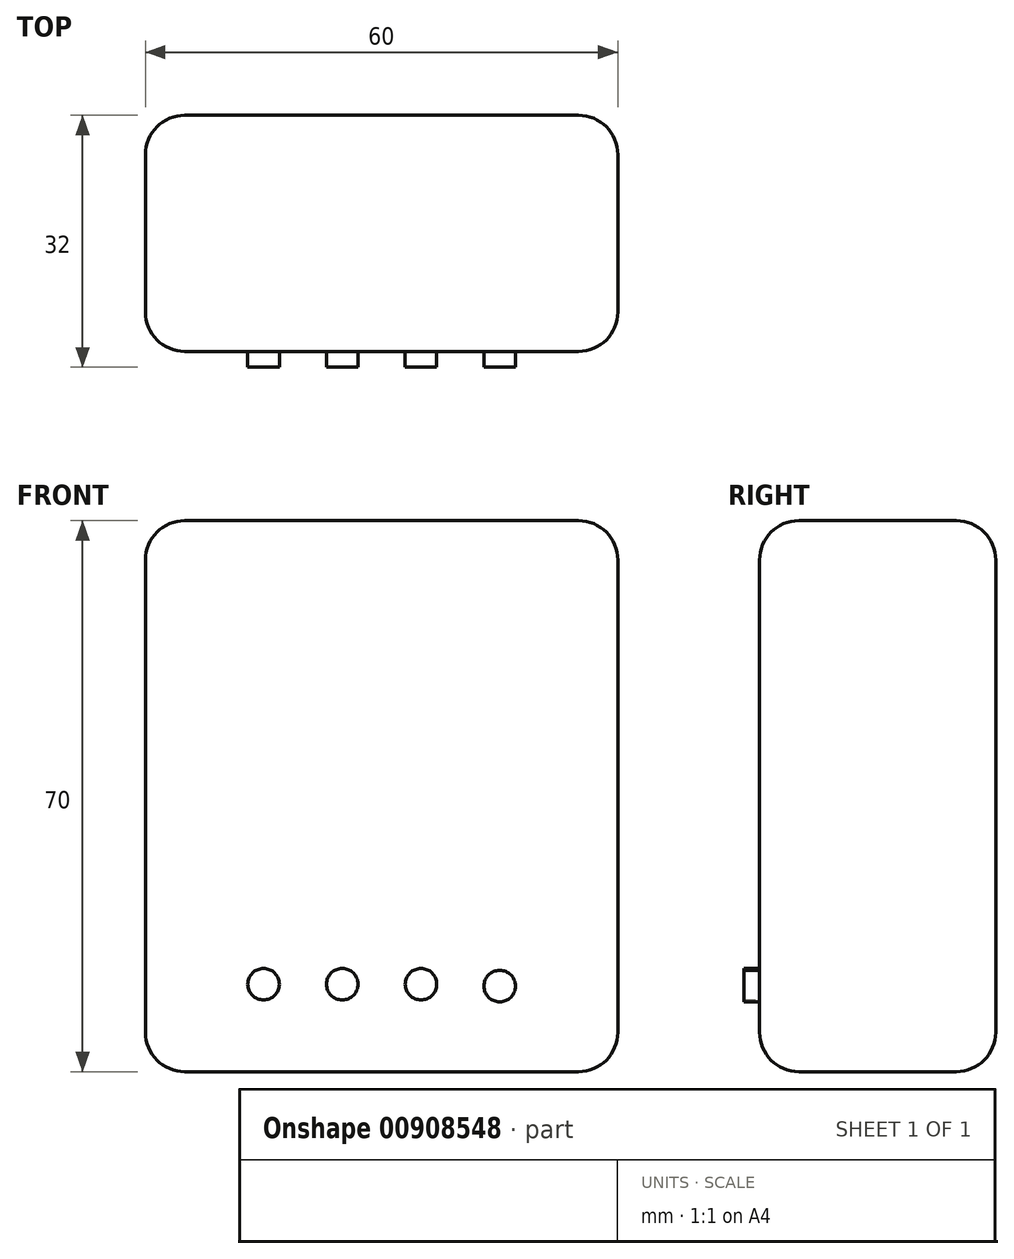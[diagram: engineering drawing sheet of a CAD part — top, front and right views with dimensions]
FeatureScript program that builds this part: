
annotation { "Feature Type Name" : "Feature", "Feature Type Description" : "" }
export const myFeature = defineFeature(function(context is Context, id is Id, definition is map)
    precondition{}
    {
        {
            var Q0;
            Q0=qCreatedBy(makeId("Front.planeOp"),FACE);
            var sketch = newSketch(context, id + "F0", { "sketchPlane" : qUnion([Q0])});
            skLineSegment(sketch, "E0.bottom", {"start": v(-30, 35) * mm, "end": v(30, 35) * mm});
            skLineSegment(sketch, "E0.top", {"start": v(-30, -35) * mm, "end": v(30, -35) * mm});
            skLineSegment(sketch, "E0.left", {"start": v(-30, 35) * mm, "end": v(-30, -35) * mm});
            skLineSegment(sketch, "E0.right", {"start": v(30, 35) * mm, "end": v(30, -35) * mm});
            skPoint(sketch, "E0.middle", {"position": v(0, 0) * mm});
            skPoint(sketch, "E1", {"position": v(-15, -23.89) * mm});
            skPoint(sketch, "E2", {"position": v(15, -24.13) * mm});
            skCircle(sketch, "E3", {"center": v(-15, -23.89) * mm, "radius": 2 * mm});
            skCircle(sketch, "E4", {"center": v(15, -24.13) * mm, "radius": 2 * mm});
            skCircle(sketch, "E5", {"center": v(-5, -23.89) * mm, "radius": 2 * mm});
            skCircle(sketch, "E6", {"center": v(5, -23.89) * mm, "radius": 2 * mm});
            skSolve(sketch);
        }
        {
            var Q0;
            Q0=makeQuery(id+"F0.imprint","IMPRINT",FACE,{"disambiguationData":[TD([[makeQuery(id+"F0.imprint","IMPRINT",EDGE,{"derivedFrom":sQuery(id+"F0.wireOp",EDGE,"E0.bottom")}),-1.0]])]});
            extrude(context, id + "F1", {"entities" : qUnion([Q0]), "depth" : 30 * mm, "offsetDistance" : 25 * mm});
        }
        {
            var Q0;
            Q0=makeQuery(id+"F0.imprint","IMPRINT",FACE,{"disambiguationData":[TD([[makeQuery(id+"F0.imprint","IMPRINT",EDGE,{"derivedFrom":sQuery(id+"F0.wireOp",EDGE,"E4")}),1.0]])]});
            var Q1;
            Q1=makeQuery(id+"F0.imprint","IMPRINT",FACE,{"disambiguationData":[TD([[makeQuery(id+"F0.imprint","IMPRINT",EDGE,{"derivedFrom":sQuery(id+"F0.wireOp",EDGE,"E6")}),1.0]])]});
            var Q2;
            Q2=makeQuery(id+"F0.imprint","IMPRINT",FACE,{"disambiguationData":[TD([[makeQuery(id+"F0.imprint","IMPRINT",EDGE,{"derivedFrom":sQuery(id+"F0.wireOp",EDGE,"E5")}),1.0]])]});
            var Q3;
            Q3=makeQuery(id+"F0.imprint","IMPRINT",FACE,{"disambiguationData":[TD([[makeQuery(id+"F0.imprint","IMPRINT",EDGE,{"derivedFrom":sQuery(id+"F0.wireOp",EDGE,"E3")}),1.0]])]});
            extrude(context, id + "F2", {"entities" : qUnion([Q0, Q1, Q2, Q3]), "operationType" : NewBodyOperationType.ADD, "depth" : 32 * mm, "offsetDistance" : 25 * mm});
        }
        {
            var Q0;
            Q0=makeQuery(id+"F1.opExtrude","SWEPT_EDGE",EDGE,{"disambiguationData":[OSD([sQuery(id+"F0.wireOp",EDGE,"E0.bottom"),sQuery(id+"F0.wireOp",EDGE,"E0.left")])]});
            var Q1;
            Q1=makeQuery(id+"F1.opExtrude","CAP_EDGE",EDGE,{"disambiguationData":[OSD([sQuery(id+"F0.wireOp",EDGE,"E0.bottom")])],"isStart":true});
            var Q2;
            Q2=makeQuery(id+"F1.opExtrude","CAP_EDGE",EDGE,{"disambiguationData":[OSD([sQuery(id+"F0.wireOp",EDGE,"E0.bottom")])],"isStart":false});
            var Q3;
            Q3=makeQuery(id+"F1.opExtrude","SWEPT_EDGE",EDGE,{"disambiguationData":[OSD([sQuery(id+"F0.wireOp",EDGE,"E0.bottom"),sQuery(id+"F0.wireOp",EDGE,"E0.right")])]});
            var Q4;
            Q4=makeQuery(id+"F1.opExtrude","CAP_EDGE",EDGE,{"disambiguationData":[OSD([sQuery(id+"F0.wireOp",EDGE,"E0.right")])],"isStart":false});
            var Q5;
            Q5=makeQuery(id+"F1.opExtrude","CAP_EDGE",EDGE,{"disambiguationData":[OSD([sQuery(id+"F0.wireOp",EDGE,"E0.left")])],"isStart":false});
            var Q6;
            Q6=makeQuery(id+"F1.opExtrude","CAP_EDGE",EDGE,{"disambiguationData":[OSD([sQuery(id+"F0.wireOp",EDGE,"E0.left")])],"isStart":true});
            var Q7;
            Q7=makeQuery(id+"F1.opExtrude","CAP_EDGE",EDGE,{"disambiguationData":[OSD([sQuery(id+"F0.wireOp",EDGE,"E0.right")])],"isStart":true});
            var Q8;
            Q8=makeQuery(id+"F1.opExtrude","CAP_EDGE",EDGE,{"disambiguationData":[OSD([sQuery(id+"F0.wireOp",EDGE,"E0.top")])],"isStart":true});
            var Q9;
            Q9=makeQuery(id+"F1.opExtrude","CAP_EDGE",EDGE,{"disambiguationData":[OSD([sQuery(id+"F0.wireOp",EDGE,"E0.top")])],"isStart":false});
            var Q10;
            Q10=makeQuery(id+"F1.opExtrude","SWEPT_EDGE",EDGE,{"disambiguationData":[OSD([sQuery(id+"F0.wireOp",EDGE,"E0.top"),sQuery(id+"F0.wireOp",EDGE,"E0.right")])]});
            var Q11;
            Q11=makeQuery(id+"F1.opExtrude","SWEPT_EDGE",EDGE,{"disambiguationData":[OSD([sQuery(id+"F0.wireOp",EDGE,"E0.top"),sQuery(id+"F0.wireOp",EDGE,"E0.left")])]});
            fillet(context, id + "F3", {"entities" : qUnion([Q0, Q1, Q2, Q3, Q4, Q5, Q6, Q7, Q8, Q9, Q10, Q11]), "radius" : 5 * mm, "tangentPropagation" : true, "allowEdgeOverflow" : false});
        }
    });
